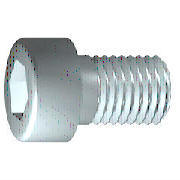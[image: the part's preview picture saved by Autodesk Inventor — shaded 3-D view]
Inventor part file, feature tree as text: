
AUTODESK INVENTOR PART (.ipt)
format: ipt  version: 2023.3 (Build 273359000, 359)  size: 185,856 bytes
history: native  units: mm (DEFAULTED — no unit token found)
features: sketch x2, other x1, extrude x1, plane x1, fillet x1
ambient origin geometry x7: Origin, YZ Plane, XY Plane, X Axis, Y Axis, Z Axis, Center Point
bodies: Solid1 (feature_tree)
feature tree (6):
  other  "Körper"
  extrude  "Loch"  Depth=2.5mm
  plane  "Work Plane1"
  fillet  "Fillet2"  Radius=2.5mm
  sketch  "Skizze1"  dims[d1=23.875mm d2=0.276153mm d3=2.5mm]
  sketch  "Skizze2"  dims[d4=1.1mm d5=60.0deg d6=2.5mm d7=2.5mm d8=2.309401mm d9=4.5mm d10=90.0deg d11=10.0mm d12=0.0mm d13=23.875mm d14=0.0mm d15=0.276052mm d16=0.276053mm d17=0.25mm d19=0.0mm d26=25.0mm d27=45.0deg d28=0.0mm d29=0.0mm d30=0.1mm]
